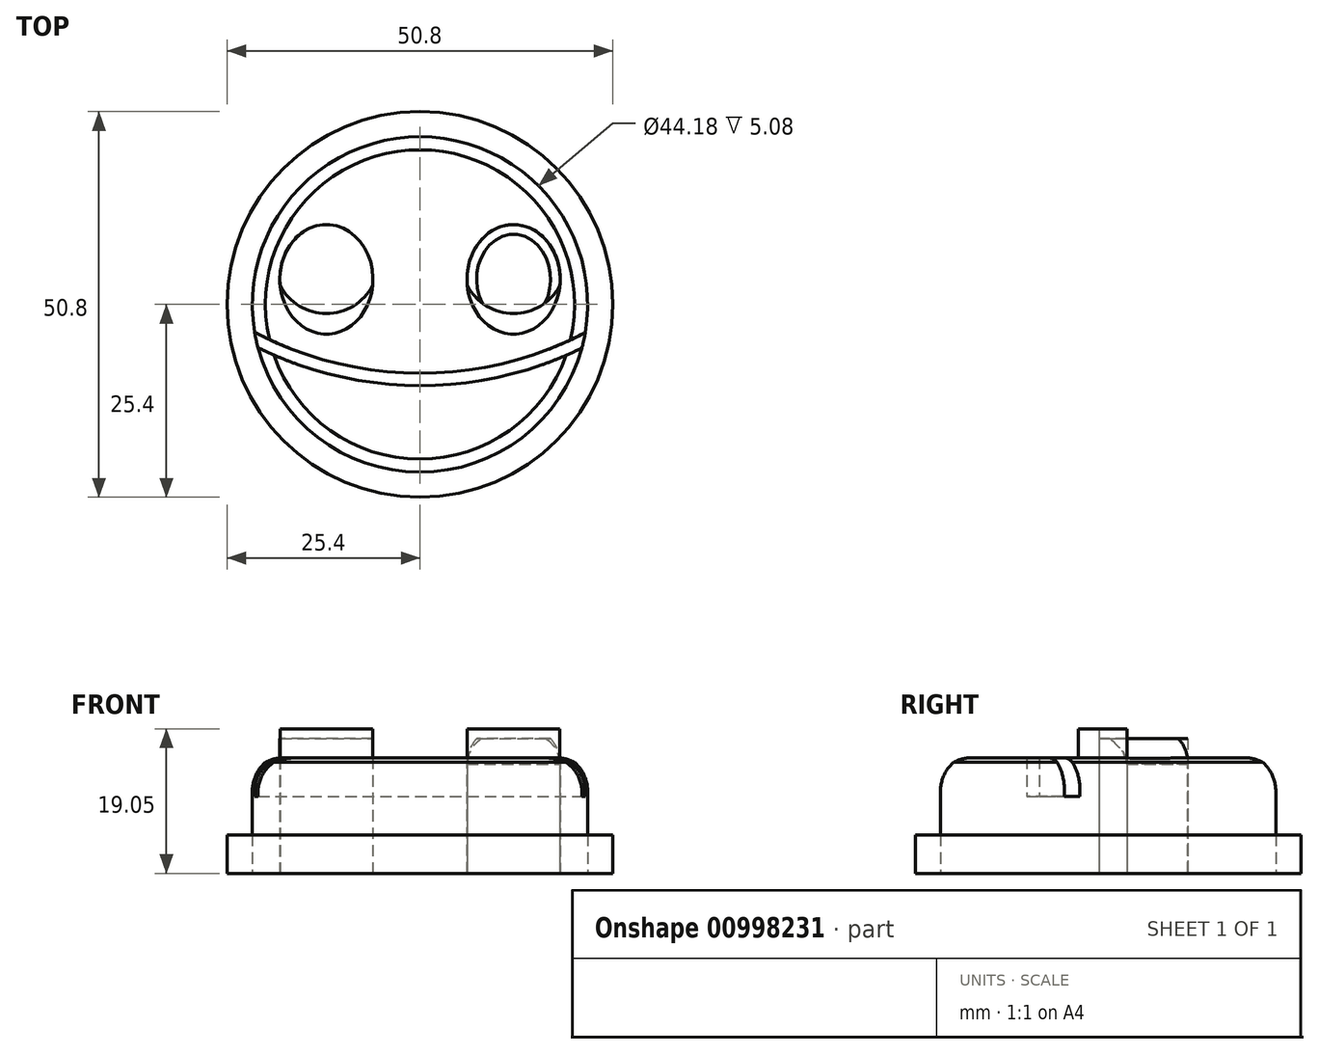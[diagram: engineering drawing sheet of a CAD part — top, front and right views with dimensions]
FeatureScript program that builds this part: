
annotation { "Feature Type Name" : "Feature", "Feature Type Description" : "" }
export const myFeature = defineFeature(function(context is Context, id is Id, definition is map)
    precondition{}
    {
        {
            var Q0;
            Q0=qCreatedBy(makeId("Top.planeOp"),FACE);
            var sketch = newSketch(context, id + "F0", { "sketchPlane" : qUnion([Q0])});
            skCircle(sketch, "E0", {"center": v(0, 0) * mm, "radius": 22.09 * mm});
            skCircle(sketch, "E1", {"center": v(0.05, 37.6) * mm, "radius": 46.67 * mm});
            skEllipse(sketch, "E2", {"center": v(-12.33, 3.31) * mm, "majorRadius": 7.21 * mm, "minorRadius": 6.14 * mm, "majorAxis": v(0, -1)});
            skCircle(sketch, "E3", {"center": v(-12.33, 5.72) * mm, "radius": 6.9 * mm});
            skCircle(sketch, "E4", {"center": v(0.05, 37.6) * mm, "radius": 48.28 * mm});
            skEllipse(sketch, "E5", {"center": v(12.33, 3.31) * mm, "majorRadius": 7.21 * mm, "minorRadius": 6.14 * mm, "majorAxis": v(0, 1)});
            skCircle(sketch, "E6", {"center": v(12.33, 5.72) * mm, "radius": 6.9 * mm});
            skCircle(sketch, "E7", {"center": v(0, 0) * mm, "radius": 25.4 * mm});
            skSolve(sketch);
        }
        {
            var Q0;
            {var subQ4=sQuery(id+"F0.wireOp",EDGE,"E0");var subQ9=sQuery(id+"F0.wireOp",EDGE,"TRHLE5c8-7O91-afYI-osa8-76lGKPRemA9O");var subQ18=makeQuery(id+"F0.imprint","INTERSECT",VERTEX,{"disambiguationData":[OD(0.0)],"derivedFrom":[subQ4,subQ9]});Q0=makeQuery(id+"F0.imprint","IMPRINT",FACE,{"disambiguationData":[TD([[makeQuery(id+"F0.imprint","IMPRINT",EDGE,{"disambiguationData":[TD([[subQ18,-1.0]])],"derivedFrom":subQ4}),1.0]])]});}
            var Q1;
            {var subQ0=sQuery(id+"F0.wireOp",EDGE,"cW8D3Qfy-Tswg-hjLe-JE63-xDJSvsmUviRl");var subQ1=sQuery(id+"F0.wireOp",EDGE,"E0");var subQ2=makeQuery(id+"F0.imprint","INTERSECT",VERTEX,{"disambiguationData":[OD(1.0)],"derivedFrom":[subQ1,subQ0]});Q1=makeQuery(id+"F0.imprint","IMPRINT",FACE,{"disambiguationData":[TD([[makeQuery(id+"F0.imprint","IMPRINT",EDGE,{"disambiguationData":[TD([[subQ2,-1.0]])],"derivedFrom":subQ1}),1.0]])]});}
            var Q2;
            {var subQ0=sQuery(id+"F0.wireOp",EDGE,"E3");var subQ1=sQuery(id+"F0.wireOp",EDGE,"E2");var subQ2=makeQuery(id+"F0.imprint","INTERSECT",VERTEX,{"disambiguationData":[OD(0.0)],"derivedFrom":[subQ1,subQ0]});Q2=makeQuery(id+"F0.imprint","IMPRINT",FACE,{"disambiguationData":[TD([[makeQuery(id+"F0.imprint","IMPRINT",EDGE,{"disambiguationData":[TD([[subQ2,-1.0]])],"derivedFrom":subQ1}),-1.0]])]});}
            var Q3;
            {var subQ0=sQuery(id+"F0.wireOp",EDGE,"Xw0NN4vq-NJnS-uVjX-KvGG-gOafCFiGMpCu");var subQ1=sQuery(id+"F0.wireOp",EDGE,"E3");var subQ2=makeQuery(id+"F0.imprint","INTERSECT",VERTEX,{"disambiguationData":[OD(0.0)],"derivedFrom":[subQ1,subQ0]});Q3=makeQuery(id+"F0.imprint","IMPRINT",FACE,{"disambiguationData":[TD([[makeQuery(id+"F0.imprint","IMPRINT",EDGE,{"disambiguationData":[TD([[subQ2,1.0]])],"derivedFrom":subQ1}),1.0]])]});}
            var Q4;
            {var subQ0=sQuery(id+"F0.wireOp",EDGE,"Xw0NN4vq-NJnS-uVjX-KvGG-gOafCFiGMpCu");var subQ1=sQuery(id+"F0.wireOp",EDGE,"E0");var subQ2=makeQuery(id+"F0.imprint","INTERSECT",VERTEX,{"disambiguationData":[OD(0.0)],"derivedFrom":[subQ1,subQ0]});Q4=makeQuery(id+"F0.imprint","IMPRINT",FACE,{"disambiguationData":[TD([[makeQuery(id+"F0.imprint","IMPRINT",EDGE,{"disambiguationData":[TD([[subQ2,-1.0]])],"derivedFrom":subQ1}),1.0]])]});}
            var Q5;
            {var subQ0=sQuery(id+"F0.wireOp",EDGE,"Xw0NN4vq-NJnS-uVjX-KvGG-gOafCFiGMpCu");var subQ1=sQuery(id+"F0.wireOp",EDGE,"E0");var subQ2=makeQuery(id+"F0.imprint","INTERSECT",VERTEX,{"disambiguationData":[OD(1.0)],"derivedFrom":[subQ1,subQ0]});Q5=makeQuery(id+"F0.imprint","IMPRINT",FACE,{"disambiguationData":[TD([[makeQuery(id+"F0.imprint","IMPRINT",EDGE,{"disambiguationData":[TD([[subQ2,-1.0]])],"derivedFrom":subQ1}),1.0]])]});}
            var Q6;
            {var subQ0=sQuery(id+"F0.wireOp",EDGE,"cW8D3Qfy-Tswg-hjLe-JE63-xDJSvsmUviRl");var subQ6=sQuery(id+"F0.wireOp",EDGE,"E0");var subQ8=makeQuery(id+"F0.imprint","INTERSECT",VERTEX,{"disambiguationData":[OD(0.0)],"derivedFrom":[subQ6,subQ0]});Q6=makeQuery(id+"F0.imprint","IMPRINT",FACE,{"disambiguationData":[TD([[makeQuery(id+"F0.imprint","IMPRINT",EDGE,{"disambiguationData":[TD([[subQ8,-1.0]])],"derivedFrom":subQ6}),1.0]])]});}
            var Q7;
            {var subQ0=sQuery(id+"F0.wireOp",EDGE,"TRHLE5c8-7O91-afYI-osa8-76lGKPRemA9O");var subQ1=sQuery(id+"F0.wireOp",EDGE,"E0");var subQ2=makeQuery(id+"F0.imprint","INTERSECT",VERTEX,{"disambiguationData":[OD(0.0)],"derivedFrom":[subQ1,subQ0]});Q7=makeQuery(id+"F0.imprint","IMPRINT",FACE,{"disambiguationData":[TD([[makeQuery(id+"F0.imprint","IMPRINT",EDGE,{"disambiguationData":[TD([[subQ2,1.0]])],"derivedFrom":subQ1}),1.0]])]});}
            var Q8;
            {var subQ0=sQuery(id+"F0.wireOp",EDGE,"TRHLE5c8-7O91-afYI-osa8-76lGKPRemA9O");var subQ1=sQuery(id+"F0.wireOp",EDGE,"E5");var subQ2=makeQuery(id+"F0.imprint","INTERSECT",VERTEX,{"disambiguationData":[OD(0.0)],"derivedFrom":[subQ1,subQ0]});Q8=makeQuery(id+"F0.imprint","IMPRINT",FACE,{"disambiguationData":[TD([[makeQuery(id+"F0.imprint","IMPRINT",EDGE,{"disambiguationData":[TD([[subQ2,1.0]])],"derivedFrom":subQ1}),-1.0]])]});}
            var Q9;
            {var subQ0=sQuery(id+"F0.wireOp",EDGE,"E6");var subQ1=sQuery(id+"F0.wireOp",EDGE,"E5");var subQ2=makeQuery(id+"F0.imprint","INTERSECT",VERTEX,{"disambiguationData":[OD(0.0)],"derivedFrom":[subQ1,subQ0]});Q9=makeQuery(id+"F0.imprint","IMPRINT",FACE,{"disambiguationData":[TD([[makeQuery(id+"F0.imprint","IMPRINT",EDGE,{"disambiguationData":[TD([[subQ2,1.0]])],"derivedFrom":subQ1}),-1.0]])]});}
            var Q10;
            {var subQ0=sQuery(id+"F0.wireOp",EDGE,"E6");var subQ1=sQuery(id+"F0.wireOp",EDGE,"E5");var subQ2=makeQuery(id+"F0.imprint","INTERSECT",VERTEX,{"disambiguationData":[OD(1.0)],"derivedFrom":[subQ1,subQ0]});Q10=makeQuery(id+"F0.imprint","IMPRINT",FACE,{"disambiguationData":[TD([[makeQuery(id+"F0.imprint","IMPRINT",EDGE,{"disambiguationData":[TD([[subQ2,-1.0]])],"derivedFrom":subQ1}),-1.0]])]});}
            var Q11;
            {var subQ0=sQuery(id+"F0.wireOp",EDGE,"E4");var subQ1=sQuery(id+"F0.wireOp",EDGE,"E0");var subQ2=makeQuery(id+"F0.imprint","INTERSECT",VERTEX,{"disambiguationData":[OD(0.0)],"derivedFrom":[subQ1,subQ0]});Q11=makeQuery(id+"F0.imprint","IMPRINT",FACE,{"disambiguationData":[TD([[makeQuery(id+"F0.imprint","IMPRINT",EDGE,{"disambiguationData":[TD([[subQ2,-1.0]])],"derivedFrom":subQ1}),1.0]])]});}
            var Q12;
            {var subQ0=sQuery(id+"F0.wireOp",EDGE,"d3hCv4XL-1LRK-furJ-uE4o-z0d2rChpYVlt");var subQ1=sQuery(id+"F0.wireOp",EDGE,"E0");var subQ2=makeQuery(id+"F0.imprint","INTERSECT",VERTEX,{"disambiguationData":[OD(0.0)],"derivedFrom":[subQ1,subQ0]});Q12=makeQuery(id+"F0.imprint","IMPRINT",FACE,{"disambiguationData":[TD([[makeQuery(id+"F0.imprint","IMPRINT",EDGE,{"disambiguationData":[TD([[subQ2,-1.0]])],"derivedFrom":subQ1}),1.0]])]});}
            var Q13;
            {var subQ0=sQuery(id+"F0.wireOp",EDGE,"d3hCv4XL-1LRK-furJ-uE4o-z0d2rChpYVlt");var subQ1=sQuery(id+"F0.wireOp",EDGE,"E1");var subQ2=makeQuery(id+"F0.imprint","INTERSECT",VERTEX,{"disambiguationData":[OD(0.0)],"derivedFrom":[subQ1,subQ0]});Q13=makeQuery(id+"F0.imprint","IMPRINT",FACE,{"disambiguationData":[TD([[makeQuery(id+"F0.imprint","IMPRINT",EDGE,{"disambiguationData":[TD([[subQ2,-1.0]])],"derivedFrom":subQ1}),1.0]])]});}
            extrude(context, id + "F1", {"entities" : qUnion([Q0, Q1, Q2, Q3, Q4, Q5, Q6, Q7, Q8, Q9, Q10, Q11, Q12, Q13]), "depth" : 15.24 * mm, "offsetDistance" : 25.4 * mm});
        }
        {
            var Q0;
            {var subQ0=sQuery(id+"F0.wireOp",EDGE,"E1");var subQ1=sQuery(id+"F0.wireOp",EDGE,"E0");var subQ2=makeQuery(id+"F0.imprint","INTERSECT",VERTEX,{"disambiguationData":[OD(0.0)],"derivedFrom":[subQ1,subQ0]});Q0=makeQuery(id+"F0.imprint","IMPRINT",FACE,{"disambiguationData":[TD([[makeQuery(id+"F0.imprint","IMPRINT",EDGE,{"disambiguationData":[TD([[subQ2,-1.0]])],"derivedFrom":subQ1}),1.0]])]});}
            var Q1;
            {var subQ0=sQuery(id+"F0.wireOp",EDGE,"E4");var subQ1=sQuery(id+"F0.wireOp",EDGE,"E0");var subQ2=makeQuery(id+"F0.imprint","INTERSECT",VERTEX,{"disambiguationData":[OD(1.0)],"derivedFrom":[subQ1,subQ0]});Q1=makeQuery(id+"F0.imprint","IMPRINT",FACE,{"disambiguationData":[TD([[makeQuery(id+"F0.imprint","IMPRINT",EDGE,{"disambiguationData":[TD([[subQ2,-1.0]])],"derivedFrom":subQ1}),1.0]])]});}
            var Q2;
            {var subQ0=sQuery(id+"F0.wireOp",EDGE,"d3hCv4XL-1LRK-furJ-uE4o-z0d2rChpYVlt");var subQ1=sQuery(id+"F0.wireOp",EDGE,"E1");var subQ2=makeQuery(id+"F0.imprint","INTERSECT",VERTEX,{"disambiguationData":[OD(0.0)],"derivedFrom":[subQ1,subQ0]});Q2=makeQuery(id+"F0.imprint","IMPRINT",FACE,{"disambiguationData":[TD([[makeQuery(id+"F0.imprint","IMPRINT",EDGE,{"disambiguationData":[TD([[subQ2,-1.0]])],"derivedFrom":subQ1}),-1.0]])]});}
            var Q3;
            {var subQ0=sQuery(id+"F0.wireOp",EDGE,"cW8D3Qfy-Tswg-hjLe-JE63-xDJSvsmUviRl");var subQ1=sQuery(id+"F0.wireOp",EDGE,"E1");var subQ2=makeQuery(id+"F0.imprint","INTERSECT",VERTEX,{"disambiguationData":[OD(1.0)],"derivedFrom":[subQ1,subQ0]});Q3=makeQuery(id+"F0.imprint","IMPRINT",FACE,{"disambiguationData":[TD([[makeQuery(id+"F0.imprint","IMPRINT",EDGE,{"disambiguationData":[TD([[subQ2,-1.0]])],"derivedFrom":subQ1}),-1.0]])]});}
            extrude(context, id + "F2", {"entities" : qUnion([Q0, Q1, Q2, Q3]), "operationType" : NewBodyOperationType.ADD, "depth" : 10.16 * mm, "offsetDistance" : 25.4 * mm});
        }
        {
            var Q0;
            {var subQ0=sQuery(id+"F0.wireOp",EDGE,"E6");var subQ1=sQuery(id+"F0.wireOp",EDGE,"E5");var subQ2=makeQuery(id+"F0.imprint","INTERSECT",VERTEX,{"disambiguationData":[OD(0.0)],"derivedFrom":[subQ1,subQ0]});Q0=makeQuery(id+"F0.imprint","IMPRINT",FACE,{"disambiguationData":[TD([[makeQuery(id+"F0.imprint","IMPRINT",EDGE,{"disambiguationData":[TD([[subQ2,-1.0]])],"derivedFrom":subQ1}),1.0]])]});}
            var Q1;
            {var subQ0=sQuery(id+"F0.wireOp",EDGE,"E3");var subQ1=sQuery(id+"F0.wireOp",EDGE,"E2");var subQ2=makeQuery(id+"F0.imprint","INTERSECT",VERTEX,{"disambiguationData":[OD(0.0)],"derivedFrom":[subQ1,subQ0]});Q1=makeQuery(id+"F0.imprint","IMPRINT",FACE,{"disambiguationData":[TD([[makeQuery(id+"F0.imprint","IMPRINT",EDGE,{"disambiguationData":[TD([[subQ2,-1.0]])],"derivedFrom":subQ1}),1.0]])]});}
            extrude(context, id + "F3", {"entities" : qUnion([Q0, Q1]), "operationType" : NewBodyOperationType.ADD, "depth" : 19.05 * mm, "offsetDistance" : 25.4 * mm});
        }
        {
            var Q0;
            {var subQ0=sQuery(id+"F0.wireOp",EDGE,"E3");var subQ1=sQuery(id+"F0.wireOp",EDGE,"E2");var subQ2=makeQuery(id+"F0.imprint","INTERSECT",VERTEX,{"disambiguationData":[OD(0.0)],"derivedFrom":[subQ1,subQ0]});Q0=makeQuery(id+"F0.imprint","IMPRINT",FACE,{"disambiguationData":[TD([[makeQuery(id+"F0.imprint","IMPRINT",EDGE,{"disambiguationData":[TD([[subQ2,1.0]])],"derivedFrom":subQ1}),1.0]])]});}
            var Q1;
            {var subQ0=sQuery(id+"F0.wireOp",EDGE,"E3");var subQ1=sQuery(id+"F0.wireOp",EDGE,"E2");var subQ2=makeQuery(id+"F0.imprint","INTERSECT",VERTEX,{"disambiguationData":[OD(1.0)],"derivedFrom":[subQ1,subQ0]});Q1=makeQuery(id+"F0.imprint","IMPRINT",FACE,{"disambiguationData":[TD([[makeQuery(id+"F0.imprint","IMPRINT",EDGE,{"disambiguationData":[TD([[subQ2,-1.0]])],"derivedFrom":subQ1}),1.0]])]});}
            var Q2;
            {var subQ0=sQuery(id+"F0.wireOp",EDGE,"cW8D3Qfy-Tswg-hjLe-JE63-xDJSvsmUviRl");var subQ1=sQuery(id+"F0.wireOp",EDGE,"E2");var subQ2=makeQuery(id+"F0.imprint","INTERSECT",VERTEX,{"disambiguationData":[OD(0.0)],"derivedFrom":[subQ1,subQ0]});Q2=makeQuery(id+"F0.imprint","IMPRINT",FACE,{"disambiguationData":[TD([[makeQuery(id+"F0.imprint","IMPRINT",EDGE,{"disambiguationData":[TD([[subQ2,1.0]])],"derivedFrom":subQ1}),1.0]])]});}
            var Q3;
            {var subQ0=sQuery(id+"F0.wireOp",EDGE,"E6");var subQ1=sQuery(id+"F0.wireOp",EDGE,"E5");var subQ2=makeQuery(id+"F0.imprint","INTERSECT",VERTEX,{"disambiguationData":[OD(0.0)],"derivedFrom":[subQ1,subQ0]});Q3=makeQuery(id+"F0.imprint","IMPRINT",FACE,{"disambiguationData":[TD([[makeQuery(id+"F0.imprint","IMPRINT",EDGE,{"disambiguationData":[TD([[subQ2,1.0]])],"derivedFrom":subQ1}),1.0]])]});}
            extrude(context, id + "F4", {"entities" : qUnion([Q0, Q1, Q2, Q3]), "depth" : 17.78 * mm, "offsetDistance" : 25.4 * mm});
        }
        {
            var Q0;
            {var subQ0=sQuery(id+"F0.wireOp",EDGE,"E4");var subQ1=sQuery(id+"F0.wireOp",EDGE,"E0");var subQ2=makeQuery(id+"F0.imprint","INTERSECT",VERTEX,{"disambiguationData":[OD(0.0)],"derivedFrom":[subQ1,subQ0]});Q0=makeQuery(id+"F0.imprint","IMPRINT",FACE,{"disambiguationData":[TD([[makeQuery(id+"F0.imprint","IMPRINT",EDGE,{"disambiguationData":[TD([[subQ2,-1.0]])],"derivedFrom":subQ1}),-1.0]])]});}
            var Q1;
            {var subQ0=sQuery(id+"F0.wireOp",EDGE,"E4");var subQ1=sQuery(id+"F0.wireOp",EDGE,"E0");var subQ2=makeQuery(id+"F0.imprint","INTERSECT",VERTEX,{"disambiguationData":[OD(0.0)],"derivedFrom":[subQ1,subQ0]});Q1=makeQuery(id+"F0.imprint","IMPRINT",FACE,{"disambiguationData":[TD([[makeQuery(id+"F0.imprint","IMPRINT",EDGE,{"disambiguationData":[TD([[subQ2,1.0]])],"derivedFrom":subQ1}),-1.0]])]});}
            var Q2;
            {var subQ0=sQuery(id+"F0.wireOp",EDGE,"E1");var subQ1=sQuery(id+"F0.wireOp",EDGE,"E0");var subQ2=makeQuery(id+"F0.imprint","INTERSECT",VERTEX,{"disambiguationData":[OD(0.0)],"derivedFrom":[subQ1,subQ0]});Q2=makeQuery(id+"F0.imprint","IMPRINT",FACE,{"disambiguationData":[TD([[makeQuery(id+"F0.imprint","IMPRINT",EDGE,{"disambiguationData":[TD([[subQ2,1.0]])],"derivedFrom":subQ1}),-1.0]])]});}
            var Q3;
            {var subQ0=sQuery(id+"F0.wireOp",EDGE,"E4");var subQ1=sQuery(id+"F0.wireOp",EDGE,"E0");var subQ2=makeQuery(id+"F0.imprint","INTERSECT",VERTEX,{"disambiguationData":[OD(1.0)],"derivedFrom":[subQ1,subQ0]});Q3=makeQuery(id+"F0.imprint","IMPRINT",FACE,{"disambiguationData":[TD([[makeQuery(id+"F0.imprint","IMPRINT",EDGE,{"disambiguationData":[TD([[subQ2,-1.0]])],"derivedFrom":subQ1}),-1.0]])]});}
            var Q4;
            {var subQ0=sQuery(id+"F0.wireOp",EDGE,"cW8D3Qfy-Tswg-hjLe-JE63-xDJSvsmUviRl");var subQ1=sQuery(id+"F0.wireOp",EDGE,"E0");var subQ2=makeQuery(id+"F0.imprint","INTERSECT",VERTEX,{"disambiguationData":[OD(1.0)],"derivedFrom":[subQ1,subQ0]});Q4=makeQuery(id+"F0.imprint","IMPRINT",FACE,{"disambiguationData":[TD([[makeQuery(id+"F0.imprint","IMPRINT",EDGE,{"disambiguationData":[TD([[subQ2,-1.0]])],"derivedFrom":subQ1}),-1.0]])]});}
            var Q5;
            {var subQ0=sQuery(id+"F0.wireOp",EDGE,"d3hCv4XL-1LRK-furJ-uE4o-z0d2rChpYVlt");var subQ1=sQuery(id+"F0.wireOp",EDGE,"E0");var subQ2=makeQuery(id+"F0.imprint","INTERSECT",VERTEX,{"disambiguationData":[OD(0.0)],"derivedFrom":[subQ1,subQ0]});Q5=makeQuery(id+"F0.imprint","IMPRINT",FACE,{"disambiguationData":[TD([[makeQuery(id+"F0.imprint","IMPRINT",EDGE,{"disambiguationData":[TD([[subQ2,-1.0]])],"derivedFrom":subQ1}),-1.0]])]});}
            var Q6;
            {var subQ0=sQuery(id+"F0.wireOp",EDGE,"TRHLE5c8-7O91-afYI-osa8-76lGKPRemA9O");var subQ1=sQuery(id+"F0.wireOp",EDGE,"E0");var subQ2=makeQuery(id+"F0.imprint","INTERSECT",VERTEX,{"disambiguationData":[OD(1.0)],"derivedFrom":[subQ1,subQ0]});Q6=makeQuery(id+"F0.imprint","IMPRINT",FACE,{"disambiguationData":[TD([[makeQuery(id+"F0.imprint","IMPRINT",EDGE,{"disambiguationData":[TD([[subQ2,1.0]])],"derivedFrom":subQ1}),-1.0]])]});}
            var Q7;
            {var subQ0=sQuery(id+"F0.wireOp",EDGE,"TRHLE5c8-7O91-afYI-osa8-76lGKPRemA9O");var subQ1=sQuery(id+"F0.wireOp",EDGE,"E0");var subQ2=makeQuery(id+"F0.imprint","INTERSECT",VERTEX,{"disambiguationData":[OD(0.0)],"derivedFrom":[subQ1,subQ0]});Q7=makeQuery(id+"F0.imprint","IMPRINT",FACE,{"disambiguationData":[TD([[makeQuery(id+"F0.imprint","IMPRINT",EDGE,{"disambiguationData":[TD([[subQ2,1.0]])],"derivedFrom":subQ1}),-1.0]])]});}
            var Q8;
            {var subQ0=sQuery(id+"F0.wireOp",EDGE,"Xw0NN4vq-NJnS-uVjX-KvGG-gOafCFiGMpCu");var subQ1=sQuery(id+"F0.wireOp",EDGE,"E0");var subQ2=makeQuery(id+"F0.imprint","INTERSECT",VERTEX,{"disambiguationData":[OD(0.0)],"derivedFrom":[subQ1,subQ0]});Q8=makeQuery(id+"F0.imprint","IMPRINT",FACE,{"disambiguationData":[TD([[makeQuery(id+"F0.imprint","IMPRINT",EDGE,{"disambiguationData":[TD([[subQ2,-1.0]])],"derivedFrom":subQ1}),-1.0]])]});}
            var Q9;
            {var subQ0=sQuery(id+"F0.wireOp",EDGE,"Xw0NN4vq-NJnS-uVjX-KvGG-gOafCFiGMpCu");var subQ1=sQuery(id+"F0.wireOp",EDGE,"E0");var subQ2=makeQuery(id+"F0.imprint","INTERSECT",VERTEX,{"disambiguationData":[OD(1.0)],"derivedFrom":[subQ1,subQ0]});Q9=makeQuery(id+"F0.imprint","IMPRINT",FACE,{"disambiguationData":[TD([[makeQuery(id+"F0.imprint","IMPRINT",EDGE,{"disambiguationData":[TD([[subQ2,-1.0]])],"derivedFrom":subQ1}),-1.0]])]});}
            var Q10;
            {var subQ0=sQuery(id+"F0.wireOp",EDGE,"TRHLE5c8-7O91-afYI-osa8-76lGKPRemA9O");var subQ1=sQuery(id+"F0.wireOp",EDGE,"E0");var subQ2=makeQuery(id+"F0.imprint","INTERSECT",VERTEX,{"disambiguationData":[OD(0.0)],"derivedFrom":[subQ1,subQ0]});Q10=makeQuery(id+"F0.imprint","IMPRINT",FACE,{"disambiguationData":[TD([[makeQuery(id+"F0.imprint","IMPRINT",EDGE,{"disambiguationData":[TD([[subQ2,-1.0]])],"derivedFrom":subQ1}),-1.0]])]});}
            var Q11;
            {var subQ0=sQuery(id+"F0.wireOp",EDGE,"cW8D3Qfy-Tswg-hjLe-JE63-xDJSvsmUviRl");var subQ1=sQuery(id+"F0.wireOp",EDGE,"E1");var subQ2=makeQuery(id+"F0.imprint","INTERSECT",VERTEX,{"disambiguationData":[OD(0.0)],"derivedFrom":[subQ1,subQ0]});Q11=makeQuery(id+"F0.imprint","IMPRINT",FACE,{"disambiguationData":[TD([[makeQuery(id+"F0.imprint","IMPRINT",EDGE,{"disambiguationData":[TD([[subQ2,1.0]])],"derivedFrom":subQ1}),-1.0]])]});}
            var Q12;
            {var subQ0=sQuery(id+"F0.wireOp",EDGE,"d3hCv4XL-1LRK-furJ-uE4o-z0d2rChpYVlt");var subQ1=sQuery(id+"F0.wireOp",EDGE,"E0");var subQ2=makeQuery(id+"F0.imprint","INTERSECT",VERTEX,{"disambiguationData":[OD(1.0)],"derivedFrom":[subQ1,subQ0]});Q12=makeQuery(id+"F0.imprint","IMPRINT",FACE,{"disambiguationData":[TD([[makeQuery(id+"F0.imprint","IMPRINT",EDGE,{"disambiguationData":[TD([[subQ2,-1.0]])],"derivedFrom":subQ1}),-1.0]])]});}
            var Q13;
            {var subQ0=sQuery(id+"F0.wireOp",EDGE,"d72b6184-2780-437f-8c1b-8e4e60e5c181");var subQ1=sQuery(id+"F0.wireOp",EDGE,"E7");var subQ2=makeQuery(id+"F0.imprint","INTERSECT",VERTEX,{"disambiguationData":[OD(0.0)],"derivedFrom":[subQ1,subQ0]});Q13=makeQuery(id+"F0.imprint","IMPRINT",FACE,{"disambiguationData":[TD([[makeQuery(id+"F0.imprint","IMPRINT",EDGE,{"disambiguationData":[TD([[subQ2,-1.0]])],"derivedFrom":subQ1}),1.0]])]});}
            extrude(context, id + "F5", {"entities" : qUnion([Q0, Q1, Q2, Q3, Q4, Q5, Q6, Q7, Q8, Q9, Q10, Q11, Q12, Q13]), "depth" : 5.08 * mm, "offsetDistance" : 25.4 * mm});
        }
        {
            var Q0;
            Q0=makeQuery(id+"F4.opExtrude","CAP_EDGE",EDGE,{"disambiguationData":[OSD([sQuery(id+"F0.wireOp",EDGE,"E5")])],"isStart":false});
            chamfer(context, id + "F6", {"entities" : qUnion([Q0]), "width" : 1.27 * mm, "tangentPropagation" : true});
        }
        {
            var Q0;
            {var subQ0=sQuery(id+"F0.wireOp",EDGE,"E1");var subQ1=sQuery(id+"F0.wireOp",EDGE,"E0");Q0=makeQuery(id+"F1.opExtrude","CAP_EDGE",EDGE,{"disambiguationData":[OSD([subQ1]),TDD([makeQuery(id+"F0.imprint","IMPRINT",EDGE,{"disambiguationData":[TD([[makeQuery(id+"F0.imprint","INTERSECT",VERTEX,{"disambiguationData":[OD(0.0)],"derivedFrom":[subQ1,subQ0]}),1.0]])],"derivedFrom":subQ1})])],"isStart":false});}
            var Q1;
            {var subQ0=sQuery(id+"F0.wireOp",EDGE,"E4");var subQ1=sQuery(id+"F0.wireOp",EDGE,"E0");Q1=makeQuery(id+"F1.opExtrude","CAP_EDGE",EDGE,{"disambiguationData":[OSD([subQ1]),TDD([makeQuery(id+"F0.imprint","IMPRINT",EDGE,{"disambiguationData":[TD([[makeQuery(id+"F0.imprint","INTERSECT",VERTEX,{"disambiguationData":[OD(0.0)],"derivedFrom":[subQ1,subQ0]}),-1.0]])],"derivedFrom":subQ1})])],"isStart":false});}
            chamfer(context, id + "F7", {"entities" : qUnion([Q0, Q1]), "chamferType" : ChamferType.OFFSET_ANGLE, "width" : 2.54 * mm, "oppositeDirection" : false, "angle" : 35 * degree, "tangentPropagation" : true});
        }
        {
            var Q0;
            {var subQ0=sQuery(id+"F0.wireOp",EDGE,"E4");var subQ1=sQuery(id+"F0.wireOp",EDGE,"E0");var subQ2=makeQuery(id+"F0.imprint","IMPRINT",EDGE,{"disambiguationData":[TD([[makeQuery(id+"F0.imprint","INTERSECT",VERTEX,{"disambiguationData":[OD(0.0)],"derivedFrom":[subQ1,subQ0]}),-1.0]])],"derivedFrom":subQ1});Q0=makeQuery(id+"F7.opChamfer","BLEND_EDGE",EDGE,{"blendedFrom":[makeQuery(id+"F1.opExtrude","CAP_EDGE",EDGE,{"disambiguationData":[OSD([subQ1]),TDD([subQ2])],"isStart":false}),makeQuery(id+"F1.opExtrude","SWEPT_FACE",FACE,{"disambiguationData":[OSD([subQ1]),TDD([subQ2])]})],"blendedInto":[makeQuery(id+"F1.opExtrude","SWEPT_FACE",FACE,{"disambiguationData":[OSD([subQ1]),TDD([subQ2])]})]});}
            var Q1;
            {var subQ0=sQuery(id+"F0.wireOp",EDGE,"E4");var subQ1=sQuery(id+"F0.wireOp",EDGE,"E0");var subQ2=sQuery(id+"F0.wireOp",EDGE,"E1");var subQ4=makeQuery(id+"F0.imprint","INTERSECT",VERTEX,{"disambiguationData":[OD(0.0)],"derivedFrom":[subQ1,subQ2]});var subQ5=makeQuery(id+"F0.imprint","IMPRINT",EDGE,{"disambiguationData":[TD([[subQ4,1.0]])],"derivedFrom":subQ1});Q1=makeQuery(id+"F7.opChamfer","BLEND_EDGE",EDGE,{"blendedFrom":[makeQuery(id+"F1.opExtrude","CAP_EDGE",EDGE,{"disambiguationData":[OSD([subQ1]),TDD([subQ5])],"isStart":false}),makeQuery(id+"F2.boolean.opBoolean","MERGE",FACE,{"derivedFrom":[makeQuery(id+"F1.opExtrude","SWEPT_FACE",FACE,{"disambiguationData":[OSD([subQ1]),TDD([subQ5])]}),makeQuery(id+"F2.opExtrude","SWEPT_FACE",FACE,{"disambiguationData":[OSD([subQ1]),TDD([makeQuery(id+"F0.imprint","IMPRINT",EDGE,{"disambiguationData":[TD([[makeQuery(id+"F0.imprint","INTERSECT",VERTEX,{"disambiguationData":[OD(0.0)],"derivedFrom":[subQ1,subQ0]}),1.0]])],"derivedFrom":subQ1})])]}),makeQuery(id+"F2.opExtrude","SWEPT_FACE",FACE,{"disambiguationData":[OSD([subQ1]),TDD([makeQuery(id+"F0.imprint","IMPRINT",EDGE,{"disambiguationData":[TD([[makeQuery(id+"F0.imprint","INTERSECT",VERTEX,{"disambiguationData":[OD(1.0)],"derivedFrom":[subQ1,subQ0]}),-1.0]])],"derivedFrom":subQ1})])]})]})],"blendedInto":[makeQuery(id+"F2.boolean.opBoolean","MERGE",FACE,{"derivedFrom":[makeQuery(id+"F1.opExtrude","SWEPT_FACE",FACE,{"disambiguationData":[OSD([subQ1]),TDD([subQ5])]}),makeQuery(id+"F2.opExtrude","SWEPT_FACE",FACE,{"disambiguationData":[OSD([subQ1]),TDD([makeQuery(id+"F0.imprint","IMPRINT",EDGE,{"disambiguationData":[TD([[makeQuery(id+"F0.imprint","INTERSECT",VERTEX,{"disambiguationData":[OD(0.0)],"derivedFrom":[subQ1,subQ0]}),1.0]])],"derivedFrom":subQ1})])]}),makeQuery(id+"F2.opExtrude","SWEPT_FACE",FACE,{"disambiguationData":[OSD([subQ1]),TDD([makeQuery(id+"F0.imprint","IMPRINT",EDGE,{"disambiguationData":[TD([[makeQuery(id+"F0.imprint","INTERSECT",VERTEX,{"disambiguationData":[OD(1.0)],"derivedFrom":[subQ1,subQ0]}),-1.0]])],"derivedFrom":subQ1})])]})]})]});}
            var Q2;
            {var subQ0=sQuery(id+"F0.wireOp",EDGE,"E1");var subQ1=sQuery(id+"F0.wireOp",EDGE,"E0");Q2=makeQuery(id+"F7.opChamfer","BLEND_EDGE",EDGE,{"disambiguationData":[OD(0.0)],"blendedFrom":[makeQuery(id+"F1.opExtrude","CAP_EDGE",EDGE,{"disambiguationData":[OSD([subQ1]),TDD([makeQuery(id+"F0.imprint","IMPRINT",EDGE,{"disambiguationData":[TD([[makeQuery(id+"F0.imprint","INTERSECT",VERTEX,{"disambiguationData":[OD(0.0)],"derivedFrom":[subQ1,subQ0]}),1.0]])],"derivedFrom":subQ1})])],"isStart":false}),makeQuery(id+"F1.opExtrude","CAP_FACE",FACE,{"disambiguationData":[OSD([subQ1,subQ0,sQuery(id+"F0.wireOp",EDGE,"E2"),sQuery(id+"F0.wireOp",EDGE,"E5")])],"isStart":false})],"blendedInto":[makeQuery(id+"F1.opExtrude","CAP_FACE",FACE,{"disambiguationData":[OSD([subQ1,subQ0,sQuery(id+"F0.wireOp",EDGE,"E2"),sQuery(id+"F0.wireOp",EDGE,"E5")])],"isStart":false})]});}
            var Q3;
            {var subQ0=sQuery(id+"F0.wireOp",EDGE,"E4");var subQ1=sQuery(id+"F0.wireOp",EDGE,"E0");Q3=makeQuery(id+"F7.opChamfer","BLEND_EDGE",EDGE,{"blendedFrom":[makeQuery(id+"F1.opExtrude","CAP_EDGE",EDGE,{"disambiguationData":[OSD([subQ1]),TDD([makeQuery(id+"F0.imprint","IMPRINT",EDGE,{"disambiguationData":[TD([[makeQuery(id+"F0.imprint","INTERSECT",VERTEX,{"disambiguationData":[OD(0.0)],"derivedFrom":[subQ1,subQ0]}),-1.0]])],"derivedFrom":subQ1})])],"isStart":false}),makeQuery(id+"F1.opExtrude","CAP_FACE",FACE,{"disambiguationData":[OSD([subQ1,subQ0])],"isStart":false})],"blendedInto":[makeQuery(id+"F1.opExtrude","CAP_FACE",FACE,{"disambiguationData":[OSD([subQ1,subQ0])],"isStart":false})]});}
            fillet(context, id + "F8", {"entities" : qUnion([Q0, Q1, Q2, Q3]), "tangentPropagation" : true, "radius" : 5.08 * mm, "defaultsChanged" : false, "vertexSettings" : [], "allowEdgeOverflow" : false});
        }
        {
            var Q0;
            {var subQ0=sQuery(id+"F0.wireOp",EDGE,"E5");Q0=makeQuery(id+"F6.opChamfer","BLEND_EDGE",EDGE,{"blendedFrom":[makeQuery(id+"F4.opExtrude","CAP_EDGE",EDGE,{"disambiguationData":[OSD([subQ0])],"isStart":false}),makeQuery(id+"F4.opExtrude","SWEPT_FACE",FACE,{"disambiguationData":[OSD([subQ0])]})],"blendedInto":[makeQuery(id+"F4.opExtrude","SWEPT_FACE",FACE,{"disambiguationData":[OSD([subQ0])]})]});}
            fillet(context, id + "F9", {"entities" : qUnion([Q0]), "tangentPropagation" : true, "radius" : 5.08 * mm, "defaultsChanged" : false, "vertexSettings" : [], "allowEdgeOverflow" : false});
        }
    });
